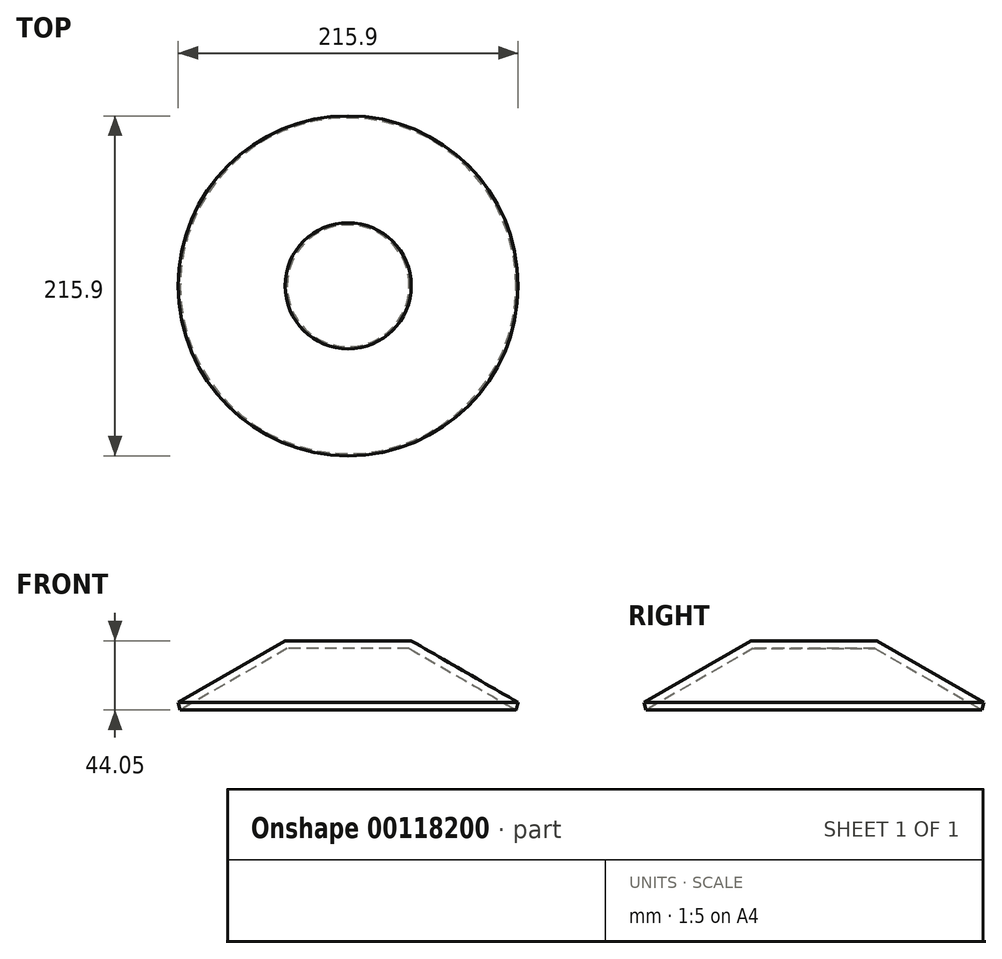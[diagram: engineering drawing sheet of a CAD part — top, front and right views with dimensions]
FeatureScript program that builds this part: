
annotation { "Feature Type Name" : "Feature", "Feature Type Description" : "" }
export const myFeature = defineFeature(function(context is Context, id is Id, definition is map)
    precondition{}
    {
        {
            var Q0;
            Q0=qCreatedBy(makeId("Front.planeOp"),FACE);
            var sketch = newSketch(context, id + "F0", { "sketchPlane" : qUnion([Q0])});
            skLineSegment(sketch, "E0", {"start": v(40, 0) * mm, "end": v(0, 0) * mm});
            skLineSegment(sketch, "E1", {"start": v(40, 0) * mm, "end": v(107.95, -39.23) * mm});
            skLineSegment(sketch, "E2.0", {"start": v(38.71, -4.83) * mm, "end": v(0, -4.83) * mm});
            skLineSegment(sketch, "E3.0", {"start": v(38.71, -4.83) * mm, "end": v(106.66, -44.05) * mm});
            skLineSegment(sketch, "E4", {"start": v(0, 0) * mm, "end": v(0, -4.83) * mm});
            skLineSegment(sketch, "E5", {"start": v(107.95, -39.23) * mm, "end": v(106.66, -44.05) * mm});
            skSolve(sketch);
        }
        {
            var Q0;
            Q0=qCreatedBy(makeId("Top.planeOp"),FACE);
            var sketch = newSketch(context, id + "F1", { "sketchPlane" : qUnion([Q0])});
            skCircle(sketch, "E6", {"center": v(0, 0) * mm, "radius": 40 * mm});
            skSolve(sketch);
        }
        {
            var Q0;
            Q0=makeQuery(id+"F0.imprint","IMPRINT",FACE,{"disambiguationData":[TD([[makeQuery(id+"F0.imprint","IMPRINT",EDGE,{"derivedFrom":sQuery(id+"F0.wireOp",EDGE,"E0")}),1.0]])]});
            var Q1;
            Q1 = qConstructionFilter(qBodyType(qCreatedBy(id + "F1" ,EDGE), BodyType.WIRE), ConstructionObject.NO);
            sweep(context, id + "F2", {"profiles" : qUnion([Q0]), "path" : qUnion([Q1])});
        }
    });
